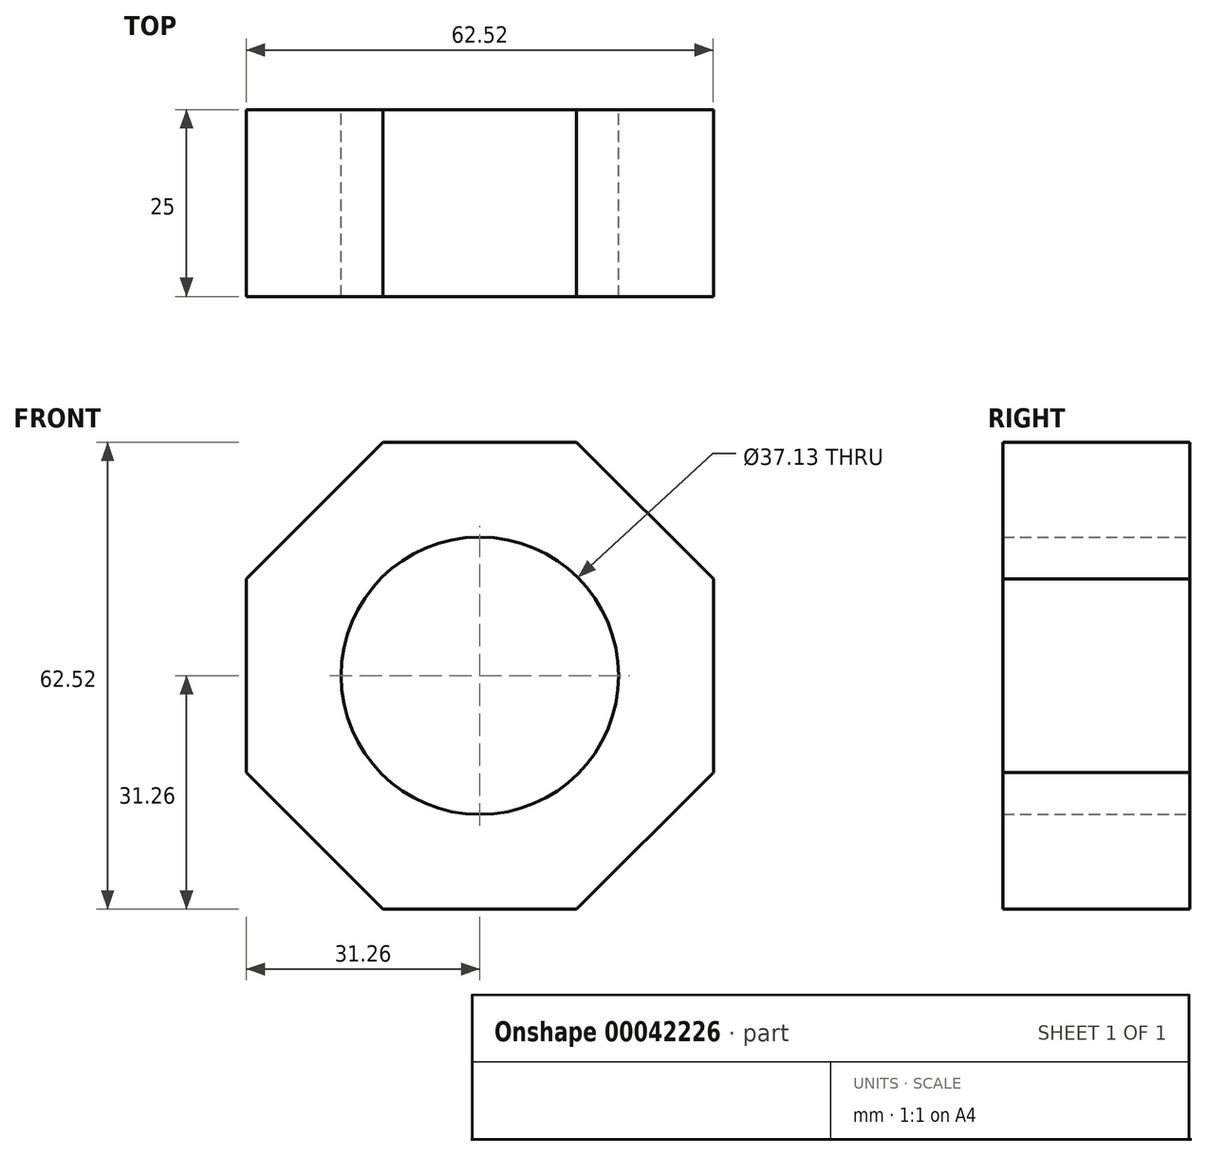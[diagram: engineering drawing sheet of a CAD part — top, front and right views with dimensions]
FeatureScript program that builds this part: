
annotation { "Feature Type Name" : "Feature", "Feature Type Description" : "" }
export const myFeature = defineFeature(function(context is Context, id is Id, definition is map)
    precondition{}
    {
        {
            var Q0;
            Q0=qCreatedBy(makeId("Front.planeOp"),FACE);
            var sketch = newSketch(context, id + "F0", { "sketchPlane" : qUnion([Q0])});
            skCircle(sketch, "E0.cCircle", {"center": v(0, 0) * mm, "radius": 31.26 * mm, "construction": true});
            skLineSegment(sketch, "E0.0", {"start": v(31.26, -12.95) * mm, "end": v(12.95, -31.26) * mm});
            skLineSegment(sketch, "E0.1", {"start": v(12.95, -31.26) * mm, "end": v(-12.95, -31.26) * mm});
            skLineSegment(sketch, "E0.2", {"start": v(-12.95, -31.26) * mm, "end": v(-31.26, -12.95) * mm});
            skLineSegment(sketch, "E0.3", {"start": v(-31.26, -12.95) * mm, "end": v(-31.26, 12.95) * mm});
            skLineSegment(sketch, "E0.4", {"start": v(-31.26, 12.95) * mm, "end": v(-12.95, 31.26) * mm});
            skLineSegment(sketch, "E0.5", {"start": v(-12.95, 31.26) * mm, "end": v(12.95, 31.26) * mm});
            skLineSegment(sketch, "E0.6", {"start": v(12.95, 31.26) * mm, "end": v(31.26, 12.95) * mm});
            skLineSegment(sketch, "E0.7", {"start": v(31.26, 12.95) * mm, "end": v(31.26, -12.95) * mm});
            skPoint(sketch, "E0.0.midPoint", {"position": v(22.1, -22.1) * mm});
            skCircle(sketch, "E1", {"center": v(0, 0) * mm, "radius": 18.56 * mm});
            skSolve(sketch);
        }
        {
            var Q0;
            Q0=makeQuery(id+"F0.imprint","IMPRINT",FACE,{"disambiguationData":[TD([[makeQuery(id+"F0.imprint","IMPRINT",EDGE,{"derivedFrom":sQuery(id+"F0.wireOp",EDGE,"E0.0")}),-1.0]])]});
            extrude(context, id + "F1", {"entities" : qUnion([Q0]), "depth" : 25 * mm});
        }
    });
